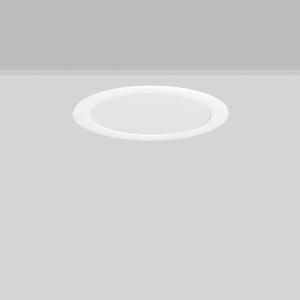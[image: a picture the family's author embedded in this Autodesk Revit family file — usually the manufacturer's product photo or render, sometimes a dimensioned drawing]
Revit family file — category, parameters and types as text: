
# Revit family: toledo_flat_round_e_672231_002_1_a98a
name_source: partatom
category: Lighting Fixtures
units: mm (PartAtom-declared; Revit-internal decimal feet)

## family parameters
Cut with Voids When Loaded = No
Host = Face
Light Source = No
Part Type = Normal
Room Calculation Point = No
Round Connector Dimension = Use Diameter
Shared = No

## types (1)
- TOLEDO FLAT round E (1 x LED Modul 840, 2250 lm, 4000)
    Apparent Load = 22 VA
    CIE Flux Codes = 49 80 96 100 100
    Color Rendering = 80
    Color Temperature = 4000
    Default Elevation = 1800 mm
    Description = Series: TOLEDO FLAT round
Ultra thin recessed downlight. For escape route illumination. Housing: die-cast aluminium, powder-coated. Lightguide and diffuser made of non-yellowing plastic (PMMA). Diffuser opal matt plastic. Ceiling installation with spring system. Including separate LED converter with connecting cable 250 mm. Suitable for connection to central battery systems. External driver with simple plug-in locking system. 
Colour: white
Diameter: 317 mm
Height: 3 mm
Cut-out diameter: 288 mm
Recess height: 35 mm
Luminaire: recess height: 31-51 mm
Weight: 1.27 kg
Operating mode: maintained power mode
Lamp: LED
Socket: without socket
Colour temperature: 4000K
Colour rendering index (CRI): 80
System power: 22 W
Rated luminous flux: 2250 lm
Luminous flux, emergency: 2250 lm
System power, emergency: 22 W
Control gear: Regulated power supply
Protection class: II
Type of protection: IP 54
    Height = 0 mm  [stored 0 ft]
    Lamp = 1 x LED Modul 840
    Lamp Light Flux = 2250 lm
    Lamp count = 1
    Length = 317 mm
    Lifetime = 50000 h
    Luminous efficacy = 102 lm/W
    Manufacturer = RZB
    ModVariant = No
    Model = 672231.002.1
    Mounting Place = Ceiling
    Mounting Type = Recessed
    Number of Poles = 1
    OnlyDefault = Yes
    Power Factor = 1
    Product Name = TOLEDO FLAT round E
    Product group = Recessed downlights
    ProductGroupID = 402
    Protection Class = Protection class II
    Protection Degree = IP 40
    RLX_Detail_Level = 1
    RLX_Emergency_Light_Flux = 2250 lm
    RLX_Emergency_Type = 3
    RLX_Emergency_Type_DB = Yes
    RlxData = <blob elided: 31325 chars, md5=2b366c9e>
    Socket = socket
    Standby Power = 0 W
    System Light Flux = 2250 lm
    System Power = 22 W
    Type Comments = Product without accessories
    Type Image = 901484.002.jpg
    URL = http://relux.com
    VarID = ---
    Voltage = 230 V
    Voltage Range = 220-240 V
    Weight = 0.00 kg
    Width = 0 mm  [stored 0 ft]

note: [stored X ft] marks values corroborated as IEEE doubles in the binary element streams (Revit-internal decimal feet)

## geometry (parser evidence)
native form markers: Blend x4, Sweep x11
no freeform markers — native parametric forms only
